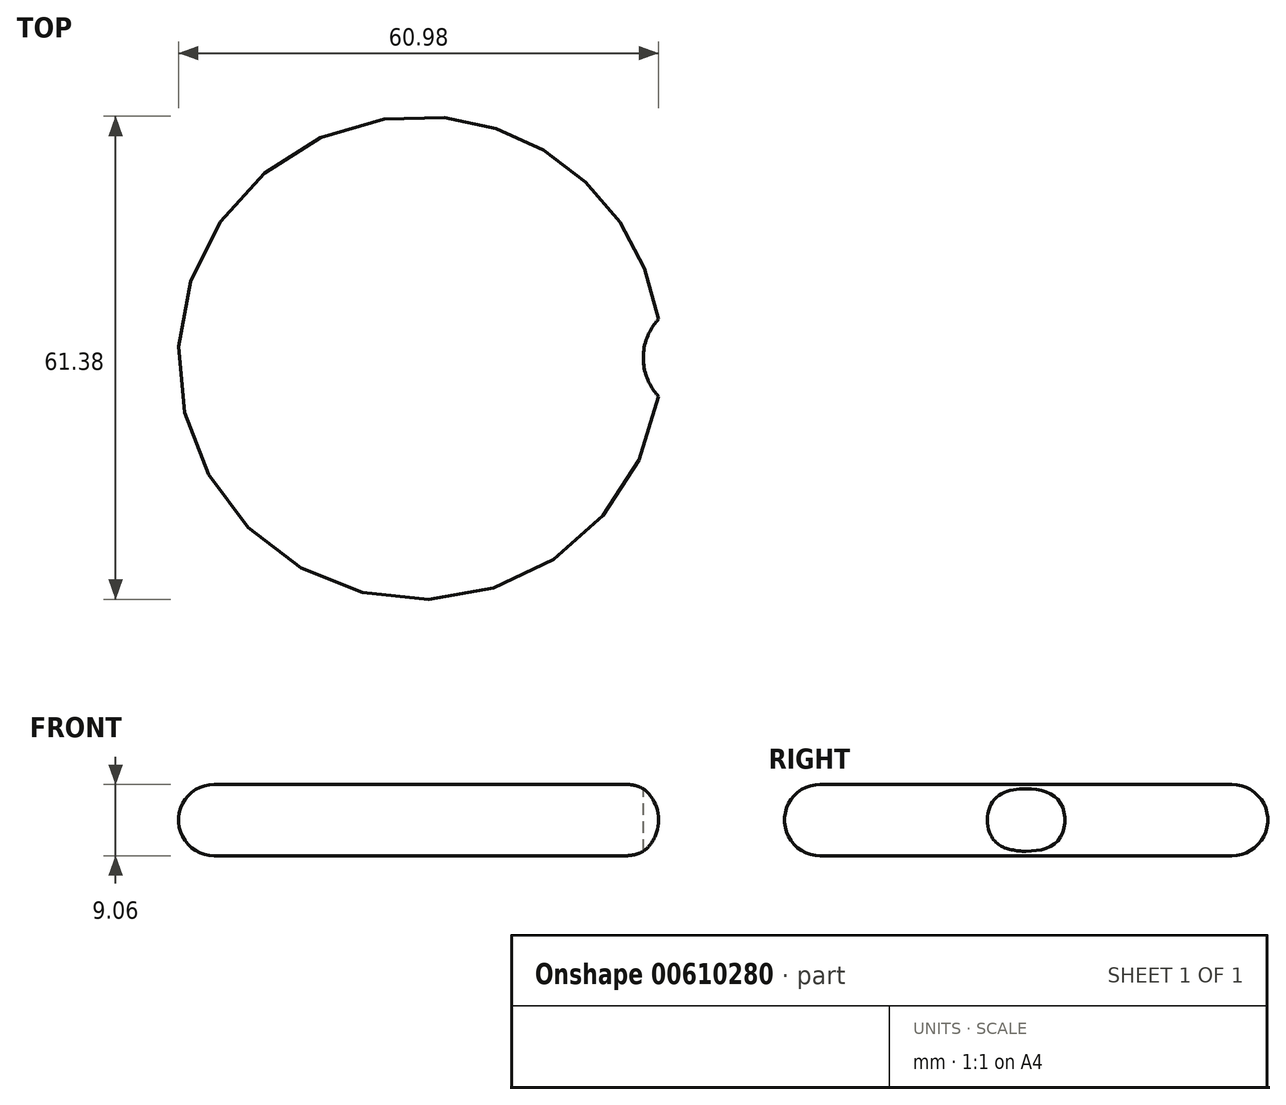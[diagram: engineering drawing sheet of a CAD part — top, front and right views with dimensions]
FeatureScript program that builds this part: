
annotation { "Feature Type Name" : "Feature", "Feature Type Description" : "" }
export const myFeature = defineFeature(function(context is Context, id is Id, definition is map)
    precondition{}
    {
        {
            var Q0;
            Q0=qCreatedBy(makeId("Front.planeOp"),FACE);
            var sketch = newSketch(context, id + "F0", { "sketchPlane" : qUnion([Q0])});
            skCircle(sketch, "E0", {"center": v(-26.16, 0) * mm, "radius": 4.53 * mm});
            skLineSegment(sketch, "E1.bottom", {"start": v(-26.16, 4.53) * mm, "end": v(0, 4.53) * mm});
            skLineSegment(sketch, "E1.top", {"start": v(-26.16, -4.53) * mm, "end": v(0, -4.53) * mm});
            skLineSegment(sketch, "E1.left", {"start": v(-26.16, 4.53) * mm, "end": v(-26.16, -4.53) * mm});
            skLineSegment(sketch, "E1.right", {"start": v(0, 4.53) * mm, "end": v(0, -4.53) * mm});
            skSolve(sketch);
        }
        {
            var Q0;
            {var subQ0=sQuery(id+"F0.wireOp",EDGE,"E1.left");Q0=makeQuery(id+"F0.imprint","IMPRINT",FACE,{"disambiguationData":[TD([[makeQuery(id+"F0.imprint","IMPRINT",EDGE,{"derivedFrom":subQ0}),1.0]])]});}
            var Q1;
            {var subQ0=sQuery(id+"F0.wireOp",EDGE,"E1.left");Q1=makeQuery(id+"F0.imprint","IMPRINT",FACE,{"disambiguationData":[TD([[makeQuery(id+"F0.imprint","IMPRINT",EDGE,{"derivedFrom":subQ0}),-1.0]])]});}
            var Q2;
            {var subQ1=sQuery(id+"F0.wireOp",EDGE,"E1.bottom");Q2=makeQuery(id+"F0.imprint","IMPRINT",FACE,{"disambiguationData":[TD([[makeQuery(id+"F0.imprint","IMPRINT",EDGE,{"derivedFrom":subQ1}),-1.0]])]});}
            var Q3;
            Q3=sQuery(id+"F0.wireOp",EDGE,"E1.right");
            revolve(context, id + "F1", {"entities" : qUnion([Q0, Q1, Q2]), "axis" : qUnion([Q3]), "revolveType" : RevolveType.FULL});
        }
        {
            var Q0;
            Q0=qCreatedBy(makeId("Top.planeOp"),FACE);
            var sketch = newSketch(context, id + "F2", { "sketchPlane" : qUnion([Q0])});
            skCircle(sketch, "E2", {"center": v(35.56, 0) * mm, "radius": 7.2 * mm});
            skSolve(sketch);
        }
        {
            var Q0;
            Q0 = qSketchRegion(id + "F2", true);
            extrude(context, id + "F3", {"entities" : qUnion([Q0]), "operationType" : NewBodyOperationType.REMOVE, "endBound" : BoundingType.SYMMETRIC, "oppositeDirection" : true, "depth" : 25.4 * mm, "offsetDistance" : 25.4 * mm});
        }
    });
